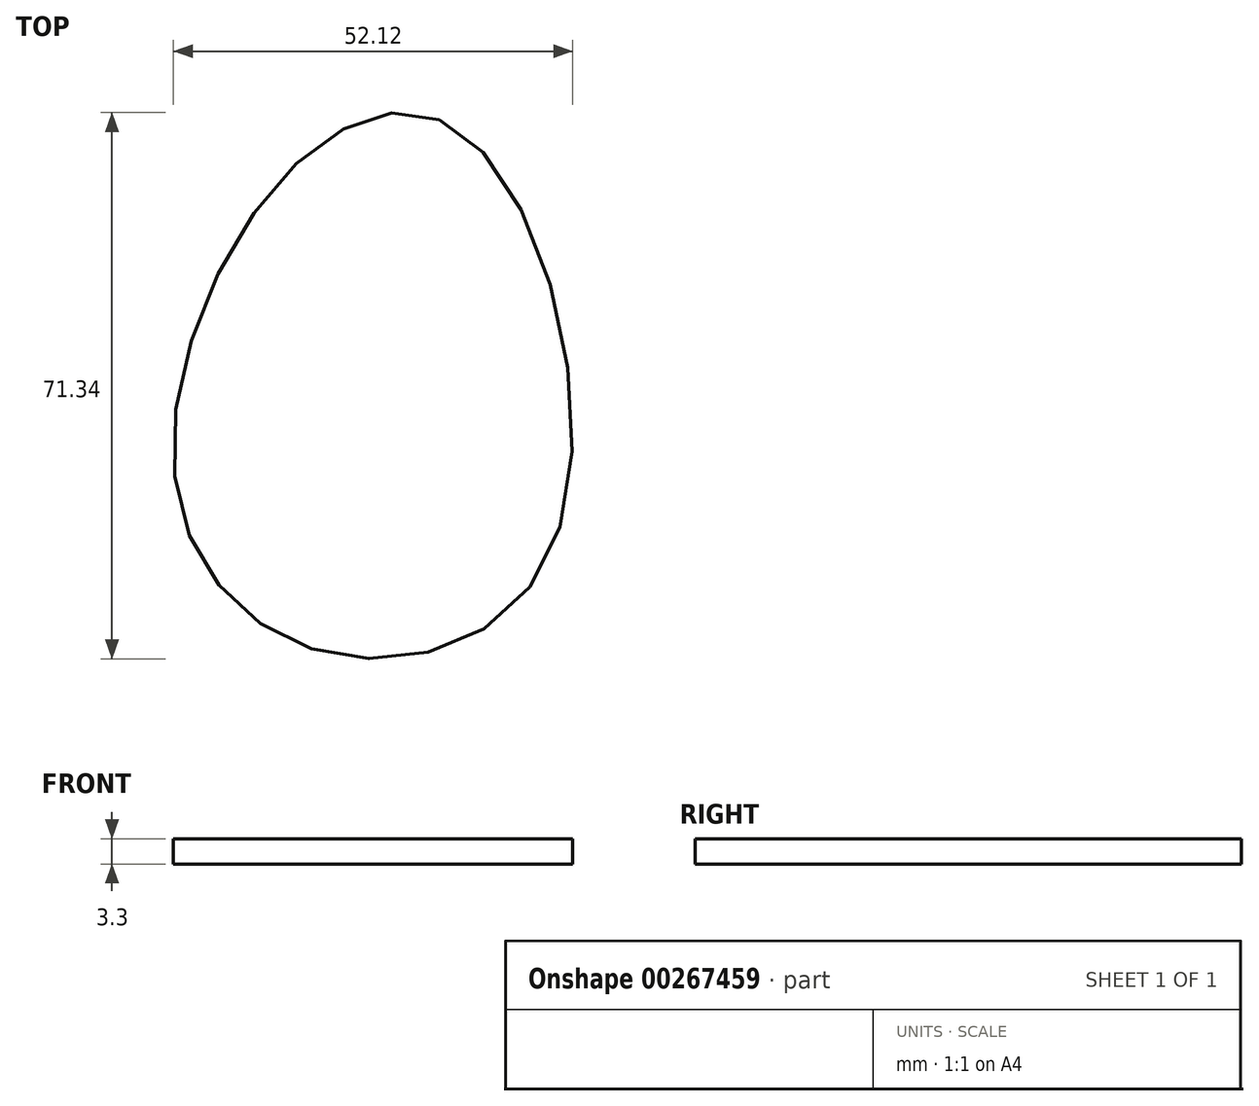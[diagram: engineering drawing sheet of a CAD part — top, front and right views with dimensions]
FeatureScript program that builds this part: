
annotation { "Feature Type Name" : "Feature", "Feature Type Description" : "" }
export const myFeature = defineFeature(function(context is Context, id is Id, definition is map)
    precondition{}
    {
        {
            var Q0;
            Q0=qCreatedBy(makeId("Top.planeOp"),FACE);
            var sketch = newSketch(context, id + "F0", { "sketchPlane" : qUnion([Q0])});
            skFitSpline(sketch, "E0", {"points": [v(-11.53, 37.77) * mm, v(-27.3, -4.1) * mm, v(-7.28, -26.24) * mm, v(21.84, -12.6) * mm, v(10.92, 41.11) * mm, v(-11.53, 37.77) * mm]});
            skSolve(sketch);
        }
        {
            var Q0;
            Q0 = qSketchRegion(id + "F0", true);
            extrude(context, id + "F1", {"entities" : qUnion([Q0]), "depth" : 3.3 * mm});
        }
    });
